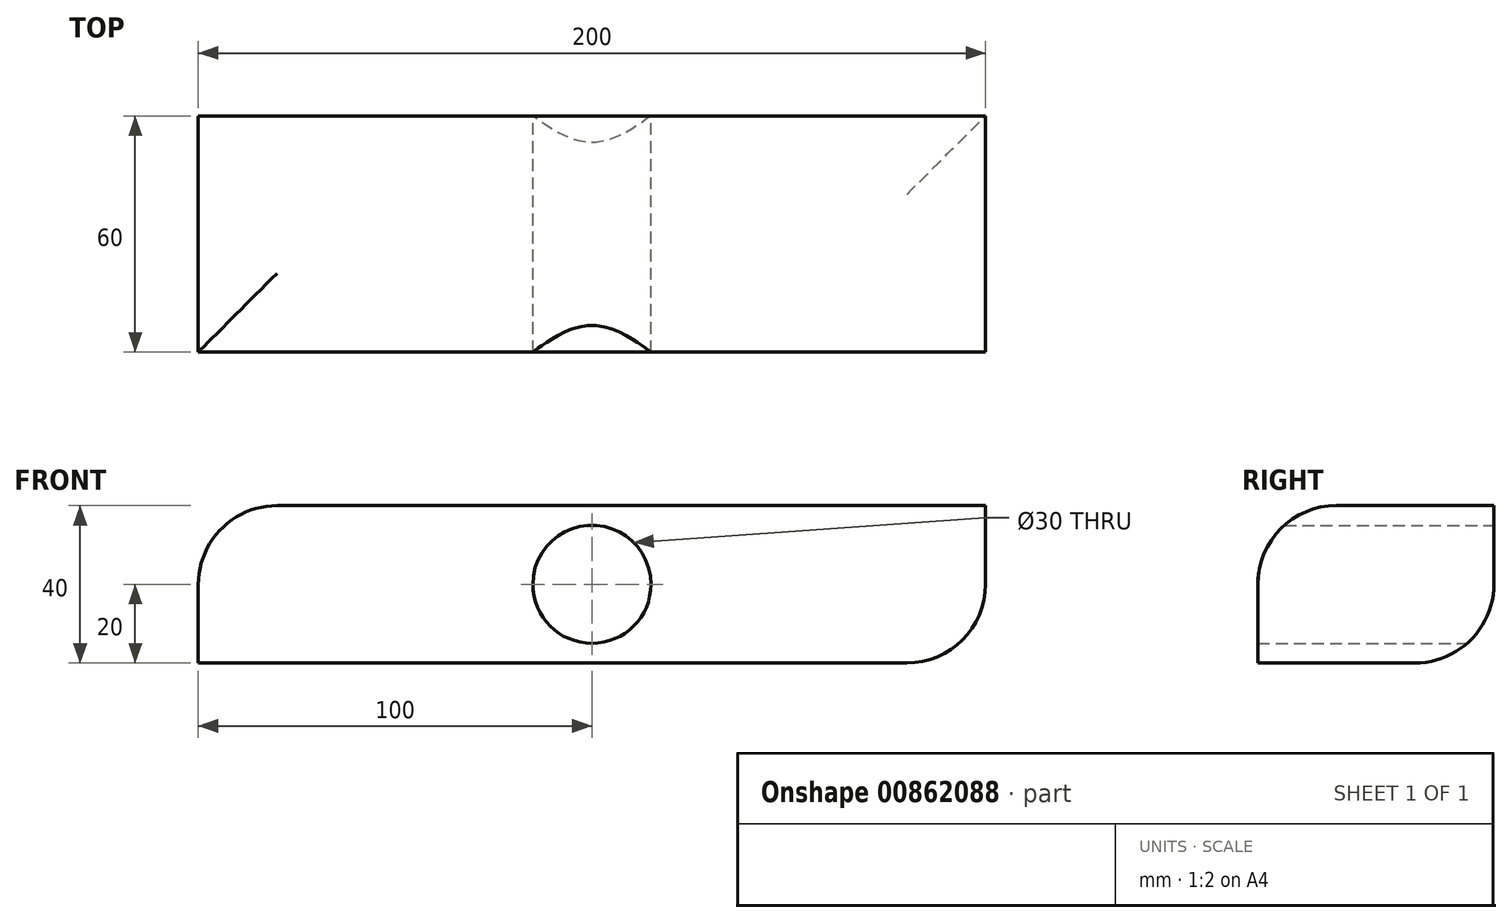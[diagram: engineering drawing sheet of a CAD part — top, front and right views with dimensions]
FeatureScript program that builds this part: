
annotation { "Feature Type Name" : "Feature", "Feature Type Description" : "" }
export const myFeature = defineFeature(function(context is Context, id is Id, definition is map)
    precondition{}
    {
        {
            var Q0;
            Q0=qCreatedBy(makeId("Front.planeOp"),FACE);
            var sketch = newSketch(context, id + "F0", { "sketchPlane" : qUnion([Q0])});
            skLineSegment(sketch, "E0.bottom", {"start": v(-200, 0) * mm, "end": v(0, 0) * mm});
            skLineSegment(sketch, "E0.top", {"start": v(-200, -40) * mm, "end": v(0, -40) * mm});
            skLineSegment(sketch, "E0.left", {"start": v(-200, 0) * mm, "end": v(-200, -40) * mm});
            skLineSegment(sketch, "E0.right", {"start": v(0, 0) * mm, "end": v(0, -40) * mm});
            skPoint(sketch, "E1", {"position": v(0, 0) * mm});
            skLineSegment(sketch, "E2", {"start": v(-200, 0) * mm, "end": v(0, -40) * mm, "construction": true});
            skCircle(sketch, "E3", {"center": v(-100, -20) * mm, "radius": 15 * mm});
            skSolve(sketch);
        }
        {
            var Q0;
            Q0 = qSketchRegion(id + "F0", true);
            extrude(context, id + "F1", {"entities" : qUnion([Q0]), "endBound" : BoundingType.SYMMETRIC, "depth" : 60 * mm, "offsetDistance" : 25.4 * mm});
        }
        {
            var Q0;
            Q0=makeQuery(id+"F1.opExtrude","SWEPT_EDGE",EDGE,{"disambiguationData":[OSD([sQuery(id+"F0.wireOp",EDGE,"E0.bottom"),sQuery(id+"F0.wireOp",EDGE,"E0.left")])]});
            var Q1;
            Q1=makeQuery(id+"F1.opExtrude","SWEPT_EDGE",EDGE,{"disambiguationData":[OSD([sQuery(id+"F0.wireOp",EDGE,"E0.top"),sQuery(id+"F0.wireOp",EDGE,"E0.right")])]});
            var Q2;
            Q2=makeQuery(id+"F1.opExtrude","CAP_EDGE",EDGE,{"disambiguationData":[OSD([sQuery(id+"F0.wireOp",EDGE,"E0.bottom")])],"isStart":false});
            var Q3;
            Q3=makeQuery(id+"F1.opExtrude","CAP_EDGE",EDGE,{"disambiguationData":[OSD([sQuery(id+"F0.wireOp",EDGE,"E0.top")])],"isStart":true});
            fillet(context, id + "F2", {"entities" : qUnion([Q0, Q1, Q2, Q3]), "radius" : 20 * mm, "tangentPropagation" : true, "allowEdgeOverflow" : false});
        }
    });
